AUTODESK INVENTOR PART (.ipt)
format: ipt  version: 2022 (Build 260153000, 153)  size: 298,496 bytes
history: native  units: in
note: dims shown in document units (in); Inventor stores cm internally (conversion verified against a paired STEP export)
features: extrude x2, other x1, sketch x1
ambient origin geometry x8: Origin, YZ Plane, XZ Plane, XY Plane, X Axis, Y Axis, Z Axis, Center Point
bodies: Body1 (feature_tree)
feature tree (4):
  other  "Sólido1"
  extrude  "Extrusión1"  Depth=0.0394in TaperAngle=0.0deg
  extrude  "Extrusión3"  Depth=0.0787in
  sketch  "Boceto3"  dims[d3=0.2559in d4=0.0in d7=0.0394in d8=0.0in d9=0.0787in d10=0.0787in]
